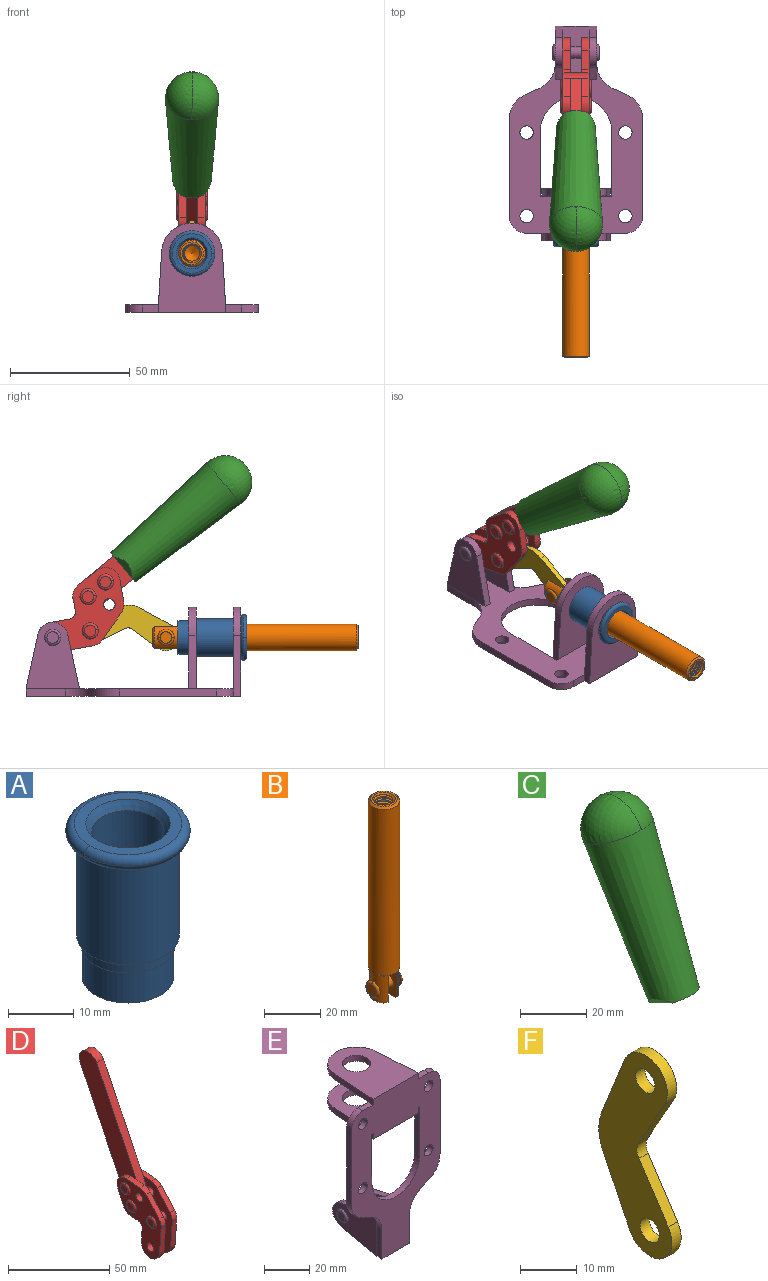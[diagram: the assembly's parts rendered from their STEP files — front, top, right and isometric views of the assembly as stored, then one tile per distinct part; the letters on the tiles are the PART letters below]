
ASSEMBLY  parts=6 mates=6
PART A: 15 faces, bbox 20.6x20.6x28.7 mm
  f0: torus R=8.26mm, axis (0,0,1), area 56.8mm2, adj f1,f10,f12
  f1: torus R=8.26mm, axis (0,0,1), area 56.8mm2, adj f0,f6,f13
  f2: cylinder r=5.59mm len=25.91mm, axis (0,0,1), area 909.6mm2, adj f3,f4
  f3: cone r=6.86mm half-angle=45deg, axis (0,0,-1), area 70.2mm2, adj f2,f14
  f4: cone r=6.47mm half-angle=30deg, axis (0,0,1), area 66.7mm2, adj f2,f13
  f5: cylinder r=7.04mm len=14.07mm, axis (0,0,1), area 252.6mm2, adj f11,f14
  f6: torus R=8.26mm, axis (0,0,1), area 56.8mm2, adj f1,f12,f13
  f7: cylinder r=7.16mm len=14.33mm, axis (0,0,1), area 91.5mm2, adj f9,f11
  f8: cylinder r=7.86mm len=18.42mm, axis (0,0,1), area 909.6mm2, adj f9,f10
  f9: plane 15.72x15.72mm, normal (0,0,-1), area 33mm2, adj f7,f8
  f10: plane 16.51x16.51mm, normal (0,0,-1), area 19.9mm2, adj f0,f8,f12
  f11: plane 14.33x14.33mm, normal (0,0,-1), area 5.7mm2, adj f5,f7
  f12: torus R=8.26mm, axis (0,0,1), area 56.8mm2, adj f0,f6,f10
  f13: plane 16.51x16.51mm, normal (0,0,1), area 82.7mm2, adj f1,f4,f6
  f14: plane 14.07x14.07mm, normal (0,0,-1), area 7.8mm2, adj f3,f5
PART B: 48 faces, bbox 12.6x11.1x86.1 mm
  f0: torus R=2.41mm, axis (-1,0,0), area 15mm2, adj f30,f32,f34
  f1: torus R=2.41mm, axis (-1,0,0), area 15mm2, adj f29,f31,f33
  f2: cylinder r=5.54mm len=72.39mm, axis (0,0,1), area 2518.5mm2, adj f3,f4,f42,f43
  f3: cone r=5.54mm half-angle=45deg, axis (0,0,1), area 7.6mm2, adj f2,f5,f41
  f4: cone r=5.54mm half-angle=45deg, axis (0,0,-1), area 34.9mm2, adj f2,f39
  f5: cylinder r=5.08mm len=11.48mm, axis (0,0,1), area 108.3mm2, adj f3,f7,f8,f41
  f6: cylinder r=2.41mm len=4.83mm, axis (-1,0,0), area 71.2mm2, adj f40,f41
  f7: cylinder r=2.41mm len=4.83mm, axis (-1,0,0), area 7.6mm2, adj f5,f34
  f8: cone r=5.08mm half-angle=45deg, axis (0,0,1), area 10.6mm2, adj f5,f37,f41
  f9: cone r=3.98mm half-angle=45deg, axis (0,0,1), area 17.6mm2, adj f27,f39,f45,f46,f47
  f10: cylinder r=2.41mm len=4.83mm, axis (-1,0,0), area 7.6mm2, adj f33,f38
  f11: cylinder r=3.2mm len=6.4mm, axis (0,0,1), area 78.4mm2, adj f12,f28,f44,f45,f47
  f12: cylinder r=3.2mm len=6.4mm, axis (0,0,1), area 10.5mm2, adj f11,f13,f45,f47
  f13: cylinder r=3.2mm len=6.4mm, axis (0,0,1), area 10.5mm2, adj f12,f14,f45,f47
  f14: cylinder r=3.2mm len=6.4mm, axis (0,0,1), area 10.5mm2, adj f13,f15,f45,f47
  f15: cylinder r=3.2mm len=6.4mm, axis (0,0,1), area 10.5mm2, adj f14,f16,f45,f47
  f16: cylinder r=3.2mm len=6.4mm, axis (0,0,1), area 10.5mm2, adj f15,f17,f45,f47
  f17: cylinder r=3.2mm len=6.4mm, axis (0,0,1), area 10.5mm2, adj f16,f18,f45,f47
  f18: cylinder r=3.2mm len=6.4mm, axis (0,0,1), area 10.5mm2, adj f17,f19,f45,f47
  f19: cylinder r=3.2mm len=6.4mm, axis (0,0,1), area 10.5mm2, adj f18,f20,f45,f47
  f20: cylinder r=3.2mm len=6.4mm, axis (0,0,1), area 10.5mm2, adj f19,f21,f45,f47
  f21: cylinder r=3.2mm len=6.4mm, axis (0,0,1), area 10.5mm2, adj f20,f22,f45,f47
  f22: cylinder r=3.2mm len=6.4mm, axis (0,0,1), area 10.5mm2, adj f21,f23,f45,f47
  f23: cylinder r=3.2mm len=6.4mm, axis (0,0,1), area 10.5mm2, adj f22,f24,f45,f47
  f24: cylinder r=3.2mm len=6.4mm, axis (0,0,1), area 10.5mm2, adj f23,f25,f45,f47
  f25: cylinder r=3.2mm len=6.4mm, axis (0,0,1), area 10.5mm2, adj f24,f26,f45,f47
  f26: cylinder r=3.2mm len=6.4mm, axis (0,0,1), area 10.5mm2, adj f25,f27,f45,f47
  f27: cylinder r=3.2mm len=6.4mm, axis (0,0,1), area 7.4mm2, adj f9,f26,f45,f47
  f28: cone r=3.2mm half-angle=60deg, axis (0,0,1), area 37.2mm2, adj f11
  f29: plane 4.83x4.83mm, normal (-1,0,0), area 18.3mm2, adj f1,f31
  f30: plane 4.83x4.83mm, normal (1,0,0), area 18.3mm2, adj f0,f32
  f31: torus R=2.41mm, axis (-1,0,0), area 15mm2, adj f1,f29,f33
  f32: torus R=2.41mm, axis (-1,0,0), area 15mm2, adj f0,f30,f34
  f33: plane 6.83x6.83mm, normal (1,0,0), area 18.3mm2, adj f1,f10,f31
  f34: plane 6.83x6.83mm, normal (-1,0,0), area 18.3mm2, adj f0,f7,f32
  f35: cone r=5.08mm half-angle=45deg, axis (0,0,1), area 10.6mm2, adj f36,f38,f40
  f36: plane 7.25x1.97mm, normal (0,0,-1), area 10mm2, adj f35,f40
  f37: plane 7.25x1.97mm, normal (0,0,-1), area 10mm2, adj f8,f41
  f38: cylinder r=5.08mm len=11.48mm, axis (0,0,1), area 108.3mm2, adj f10,f35,f40,f42
  f39: plane 9.55x9.55mm, normal (0,0,1), area 22mm2, adj f4,f9
  f40: plane 12.76x10.09mm, normal (1,0,0), area 95.7mm2, adj f6,f35,f36,f38,f42,f43
  f41: plane 12.76x10.09mm, normal (-1,0,0), area 95.7mm2, adj f3,f5,f6,f8,f37,f43
  f42: cone r=5.54mm half-angle=45deg, axis (0,0,1), area 7.6mm2, adj f2,f38,f40
  f43: plane 11.07x4.7mm, normal (0,0,-1), area 50.4mm2, adj f2,f40,f41
  f44: plane 0.89x0.62mm, normal (-1,0,0), area 0.3mm2, adj f11,f45,f46,f47
  f45: bspline ~24.8x7.63mm, area 266.6mm2, adj f9,f11,f12,f13,f14,f15,f16,f17
  f46: bspline ~24.87x7.63mm, area 73.6mm2, adj f9,f44,f45,f47
  f47: bspline ~24.98x7.63mm, area 272.5mm2, adj f9,f11,f12,f13,f14,f15,f16,f17
PART C: 11 faces, bbox 22.3x42.6x64.5 mm
  f0: sphere r=11.13mm, area 411.4mm2, adj f1,f8
  f1: cone r=11.11mm half-angle=3.3deg, axis (0,0.44,0.9), area 3251.8mm2, adj f0,f7,f8,f9,f10
  f2: cylinder r=6.16mm len=11.7mm, axis (1,0,0), area 89.5mm2, adj f3,f4,f5,f6
  f3: plane 60.23x36.75mm, normal (-1,0,0), area 763.6mm2, adj f2,f4,f6,f10
  f4: plane 51.37x25.05mm, normal (0,0.9,-0.44), area 264.2mm2, adj f2,f3,f5,f10
  f5: plane 60.23x36.75mm, normal (1,0,0), area 763.6mm2, adj f2,f4,f6,f10
  f6: plane 51.37x25.05mm, normal (0,-0.9,0.44), area 264.2mm2, adj f2,f3,f5,f10
  f7: plane 9.95x5.95mm, normal (0.71,-0.31,-0.64), area 25.8mm2, adj f1,f10
  f8: sphere r=11.13mm, area 411.4mm2, adj f0,f1
  f9: plane 9.95x5.95mm, normal (-0.71,-0.31,-0.64), area 25.8mm2, adj f1,f10
  f10: plane 14.27x11.38mm, normal (0,-0.44,-0.9), area 106.7mm2, adj f1,f3,f4,f5,f6,f7,f9
PART D: 59 faces, bbox 12.9x60.2x99.6 mm
  f0: torus R=2.39mm, axis (-1,0,0), area 14.9mm2, adj f20,f43,f51
  f1: torus R=2.39mm, axis (-1,0,0), area 14.9mm2, adj f19,f42,f51
  f2: torus R=2.39mm, axis (-1,0,0), area 14.9mm2, adj f18,f35,f51
  f3: torus R=2.39mm, axis (-1,0,0), area 14.9mm2, adj f14,f17,f23
  f4: torus R=2.39mm, axis (-1,0,0), area 14.9mm2, adj f13,f16,f23
  f5: torus R=2.39mm, axis (-1,0,0), area 14.9mm2, adj f12,f15,f23
  f6: cylinder r=2.39mm len=4.78mm, axis (1,0,0), area 46.5mm2, adj f48,f50,f51
  f7: cylinder r=2.39mm len=4.78mm, axis (1,0,0), area 46.5mm2, adj f50,f51
  f8: cylinder r=6.35mm len=12.68mm, axis (1,0,0), area 61.8mm2, adj f38,f39,f50,f51
  f9: cylinder r=2.39mm len=4.78mm, axis (-1,0,0), area 70.5mm2, adj f46,f50
  f10: cylinder r=2.39mm len=4.78mm, axis (-1,0,0), area 46.5mm2, adj f23,f45,f46
  f11: cylinder r=2.39mm len=4.78mm, axis (-1,0,0), area 46.5mm2, adj f23,f46
  f12: plane 4.78x4.78mm, normal (1,0,0), area 17.9mm2, adj f5,f15
  f13: plane 4.78x4.78mm, normal (1,0,0), area 17.9mm2, adj f4,f16
  f14: plane 4.78x4.78mm, normal (1,0,0), area 17.9mm2, adj f3,f17
  f15: torus R=2.39mm, axis (-1,0,0), area 14.9mm2, adj f5,f12,f23
  f16: torus R=2.39mm, axis (-1,0,0), area 14.9mm2, adj f4,f13,f23
  f17: torus R=2.39mm, axis (-1,0,0), area 14.9mm2, adj f3,f14,f23
  f18: plane 4.78x4.78mm, normal (-1,0,0), area 17.9mm2, adj f2,f35
  f19: plane 4.78x4.78mm, normal (-1,0,0), area 17.9mm2, adj f1,f42
  f20: plane 4.78x4.78mm, normal (-1,0,0), area 17.9mm2, adj f0,f43
  f21: plane 2.26x0.2mm, normal (1,0,0), area 0.2mm2, adj f31,f44
  f22: plane 2.26x0.2mm, normal (-1,0,0), area 0.2mm2, adj f41,f44
  f23: plane 39.37x30.77mm, normal (1,0,0), area 565.5mm2, adj f3,f4,f5,f10,f11,f15,f16,f17
  f24: cylinder r=6.1mm len=4.15mm, axis (-1,0,0), area 14.7mm2, adj f23,f25,f32,f46
  f25: plane 10.25x9.01mm, normal (0,-0.75,0.66), area 42.3mm2, adj f23,f24,f26,f46
  f26: cylinder r=6.35mm len=4.64mm, axis (-1,0,0), area 15.6mm2, adj f23,f25,f27,f46
  f27: plane 15.84x3.1mm, normal (0,-1,-0.07), area 49.2mm2, adj f23,f26,f28,f46
  f28: cylinder r=6.35mm len=12.68mm, axis (-1,0,0), area 61.8mm2, adj f23,f27,f29,f46
  f29: plane 8.11x3.1mm, normal (0,1,0.07), area 25.2mm2, adj f23,f28,f30,f46
  f30: cylinder r=3.05mm len=3.25mm, axis (-1,0,0), area 14.8mm2, adj f23,f29,f31,f46
  f31: plane 5.99x3.1mm, normal (0,0.07,-1), area 18.6mm2, adj f21,f23,f30,f44,f46
  f32: plane 9.5x3.1mm, normal (0,-0.07,1), area 29.5mm2, adj f23,f24,f33,f46,f47
  f33: cylinder r=6.1mm len=8.63mm, axis (-1,0,0), area 39.1mm2, adj f23,f32,f34,f47
  f34: plane 8.65x3.96mm, normal (0,0.91,-0.42), area 29.5mm2, adj f23,f33,f44,f47
  f35: torus R=2.39mm, axis (-1,0,0), area 14.9mm2, adj f2,f18,f51
  f36: plane 10.25x9.01mm, normal (0,-0.75,0.66), area 42.3mm2, adj f37,f49,f50,f51
  f37: cylinder r=6.35mm len=4.64mm, axis (1,0,0), area 15.6mm2, adj f36,f38,f50,f51
  f38: plane 15.84x3.1mm, normal (0,-1,-0.07), area 49.2mm2, adj f8,f37,f50,f51
  f39: plane 8.11x3.1mm, normal (0,1,0.07), area 25.2mm2, adj f8,f40,f50,f51
  f40: cylinder r=3.05mm len=3.25mm, axis (1,0,0), area 14.8mm2, adj f39,f41,f50,f51
  f41: plane 5.99x3.1mm, normal (0,0.07,-1), area 18.6mm2, adj f22,f40,f44,f50,f51
  f42: torus R=2.39mm, axis (-1,0,0), area 14.9mm2, adj f1,f19,f51
  f43: torus R=2.39mm, axis (-1,0,0), area 14.9mm2, adj f0,f20,f51
  f44: cylinder r=6.35mm len=12.12mm, axis (-1,0,0), area 128.9mm2, adj f21,f22,f23,f31,f34,f41,f46,f47
  f45: plane 2.65x1.35mm, normal (1,0,0), area 1mm2, adj f10,f55
  f46: plane 39.08x20.42mm, normal (-1,0,0), area 412.5mm2, adj f9,f10,f11,f24,f25,f26,f27,f28
  f47: plane 77.62x39.82mm, normal (1,0,0), area 850mm2, adj f32,f33,f34,f44,f53,f54,f55
  f48: plane 2.65x1.35mm, normal (-1,0,0), area 1mm2, adj f6,f55
  f49: cylinder r=6.1mm len=4.15mm, axis (1,0,0), area 14.7mm2, adj f36,f50,f51,f56
  f50: plane 39.08x20.42mm, normal (1,0,0), area 412.5mm2, adj f6,f7,f8,f9,f36,f37,f38,f39
  f51: plane 39.37x30.77mm, normal (-1,0,0), area 565.5mm2, adj f0,f1,f2,f6,f7,f8,f35,f36
  f52: plane 8.65x3.96mm, normal (0,0.91,-0.42), area 29.5mm2, adj f44,f51,f57,f58
  f53: plane 68.49x33.4mm, normal (0,0.9,-0.44), area 358.1mm2, adj f44,f47,f54,f58
  f54: cylinder r=6.35mm len=12.06mm, axis (1,0,0), area 93.7mm2, adj f47,f53,f55,f58
  f55: plane 68.49x33.4mm, normal (0,-0.9,0.44), area 358.1mm2, adj f44,f45,f46,f47,f48,f50,f54,f58
  f56: plane 9.5x3.1mm, normal (0,-0.07,1), area 29.5mm2, adj f49,f50,f51,f57,f58
  f57: cylinder r=6.1mm len=8.63mm, axis (1,0,0), area 39.1mm2, adj f51,f52,f56,f58
  f58: plane 77.62x39.82mm, normal (-1,0,0), area 850mm2, adj f44,f52,f53,f54,f55,f56,f57
PART E: 55 faces, bbox 55.7x37.4x89.8 mm
  f0: torus R=2.41mm, axis (-1,0,0), area 15mm2, adj f11,f15,f25
  f1: torus R=2.41mm, axis (-1,0,0), area 15mm2, adj f10,f12,f22
  f2: cylinder r=2.78mm len=5.56mm, axis (0,-1,0), area 54.2mm2, adj f30,f54
  f3: cylinder r=14.99mm len=29.97mm, axis (0,-1,0), area 145.9mm2, adj f30,f49,f53,f54
  f4: cylinder r=2.78mm len=5.56mm, axis (0,-1,0), area 54.2mm2, adj f30,f54
  f5: cylinder r=2.78mm len=5.56mm, axis (0,-1,0), area 54.2mm2, adj f30,f54
  f6: cylinder r=2.78mm len=5.56mm, axis (0,-1,0), area 54.2mm2, adj f30,f54
  f7: cylinder r=6.35mm len=12.7mm, axis (0,0,1), area 123.6mm2, adj f27,f51
  f8: cylinder r=6.35mm len=12.7mm, axis (0,0,-1), area 124.7mm2, adj f21,f35
  f9: cylinder r=2.41mm len=11.18mm, axis (-1,0,0), area 169.4mm2, adj f16,f19
  f10: plane 4.83x4.83mm, normal (1,0,0), area 18.3mm2, adj f1,f12
  f11: plane 4.83x4.83mm, normal (-1,0,0), area 18.3mm2, adj f0,f15
  f12: torus R=2.41mm, axis (-1,0,0), area 15mm2, adj f1,f10,f22
  f13: cylinder r=6.35mm len=12.41mm, axis (1,0,0), area 53.4mm2, adj f18,f19,f22,f23
  f14: cylinder r=6.35mm len=12.41mm, axis (-1,0,0), area 53.4mm2, adj f16,f17,f24,f25
  f15: torus R=2.41mm, axis (-1,0,0), area 15mm2, adj f0,f11,f25
  f16: plane 27.86x22.35mm, normal (1,0,0), area 425.4mm2, adj f9,f14,f17,f24,f30
  f17: plane 22.86x4.97mm, normal (0,0.21,0.98), area 72.5mm2, adj f14,f16,f25,f30
  f18: plane 22.86x4.97mm, normal (0,0.21,0.98), area 72.5mm2, adj f13,f19,f22,f30
  f19: plane 27.86x22.35mm, normal (-1,0,0), area 425.4mm2, adj f9,f13,f18,f23,f30
  f20: cylinder r=12.7mm len=25.35mm, axis (0,0,-1), area 119.8mm2, adj f21,f34,f35,f36
  f21: plane 34.21x28.07mm, normal (0,0,-1), area 702.4mm2, adj f8,f20,f30,f34,f36
  f22: plane 27.96x22.45mm, normal (1,0,0), area 407.2mm2, adj f1,f12,f13,f18,f23,f30,f42,f43
  f23: plane 22.86x4.97mm, normal (0,0.21,-0.98), area 72.5mm2, adj f13,f19,f22,f44
  f24: plane 22.86x4.97mm, normal (0,0.21,-0.98), area 72.5mm2, adj f14,f16,f25,f44
  f25: plane 27.86x22.35mm, normal (-1,0,0), area 407.1mm2, adj f0,f14,f15,f17,f24,f30,f45,f46
  f26: plane 3.1x0.95mm, normal (0,0,-1), area 2.7mm2, adj f30,f49,f50,f54
  f27: plane 34.21x28.07mm, normal (0,0,1), area 702.4mm2, adj f7,f28,f30,f50,f52
  f28: cylinder r=12.7mm len=25.35mm, axis (0,0,1), area 118.8mm2, adj f27,f50,f51,f52
  f29: plane 3.1x0.95mm, normal (0,0,-1), area 2.7mm2, adj f30,f52,f53,f54
  f30: plane 86.54x55.63mm, normal (0,1,0), area 2362.9mm2, adj f2,f3,f4,f5,f6,f16,f17,f18
  f31: plane 40.56x3.1mm, normal (-1,0,0), area 125.7mm2, adj f30,f32,f48,f54
  f32: cylinder r=7.11mm len=7.11mm, axis (0,-1,0), area 34.6mm2, adj f30,f31,f33,f54
  f33: plane 6.67x3.1mm, normal (0,0,1), area 20.4mm2, adj f30,f32,f34,f54
  f34: plane 25.39x3.13mm, normal (-1,0.06,0), area 79.5mm2, adj f20,f21,f33,f35,f54
  f35: plane 37.31x28.45mm, normal (0,0,1), area 789.9mm2, adj f8,f20,f34,f36,f54
  f36: plane 25.39x3.13mm, normal (1,0.06,0), area 79.5mm2, adj f20,f21,f35,f37,f54
  f37: plane 6.67x3.1mm, normal (0,0,1), area 20.4mm2, adj f30,f36,f38,f54
  f38: cylinder r=7.11mm len=7.11mm, axis (0,-1,0), area 34.6mm2, adj f30,f37,f39,f54
  f39: plane 40.56x3.1mm, normal (1,0,0), area 125.7mm2, adj f30,f38,f40,f54
  f40: cylinder r=11.18mm len=10.16mm, axis (0,-1,0), area 39.5mm2, adj f30,f39,f41,f54
  f41: plane 6.09x3.1mm, normal (0.42,0,-0.91), area 20.8mm2, adj f30,f40,f42,f54
  f42: cylinder r=11.18mm len=9.41mm, axis (0,-1,0), area 37.2mm2, adj f22,f30,f41,f43,f54
  f43: plane 16.5x3.1mm, normal (1,0,0), area 51.1mm2, adj f22,f42,f44,f54
  f44: plane 17.37x3.1mm, normal (0,0,-1), area 53.8mm2, adj f23,f24,f30,f43,f45,f54
  f45: plane 16.5x3.1mm, normal (-1,0,0), area 51.1mm2, adj f25,f44,f46,f54
  f46: cylinder r=11.18mm len=9.41mm, axis (0,-1,0), area 37.2mm2, adj f25,f30,f45,f47,f54
  f47: plane 6.09x3.1mm, normal (-0.42,0,-0.91), area 20.8mm2, adj f30,f46,f48,f54
  f48: cylinder r=11.18mm len=10.16mm, axis (0,-1,0), area 39.5mm2, adj f30,f31,f47,f54
  f49: plane 26.54x3.1mm, normal (-1,0,0), area 82.3mm2, adj f3,f26,f30,f54
  f50: plane 25.39x3.1mm, normal (1,0.06,0), area 78.8mm2, adj f26,f27,f28,f51,f54
  f51: plane 37.31x28.45mm, normal (0,0,-1), area 789.9mm2, adj f7,f28,f50,f52,f54
  f52: plane 25.39x3.1mm, normal (-1,0.06,0), area 78.8mm2, adj f27,f28,f29,f51,f54
  f53: plane 26.54x3.1mm, normal (1,0,0), area 82.3mm2, adj f3,f29,f30,f54
  f54: plane 89.66x55.63mm, normal (0,-1,0), area 2678.5mm2, adj f2,f3,f4,f5,f6,f26,f29,f31
PART F: 12 faces, bbox 2.3x18.2x42.8 mm
  f0: cylinder r=2.4mm len=4.8mm, axis (1,0,0), area 34.9mm2, adj f4,f11
  f1: cylinder r=10.41mm len=8.47mm, axis (1,0,0), area 20.2mm2, adj f4,f9,f10,f11
  f2: cylinder r=3.05mm len=3.16mm, axis (1,0,0), area 7.7mm2, adj f4,f6,f7,f11
  f3: cylinder r=2.4mm len=4.8mm, axis (1,0,0), area 34.9mm2, adj f4,f11
  f4: plane 42.81x18.23mm, normal (-1,0,0), area 414.1mm2, adj f0,f1,f2,f3,f5,f6,f7,f8
  f5: cylinder r=5.54mm len=10.67mm, axis (1,0,0), area 41.8mm2, adj f4,f6,f10,f11
  f6: plane 11.66x6.53mm, normal (0,-0.87,-0.49), area 30.9mm2, adj f2,f4,f5,f11
  f7: plane 11.17x7.33mm, normal (0,-0.84,0.55), area 30.9mm2, adj f2,f4,f8,f11
  f8: cylinder r=5.54mm len=10.51mm, axis (1,0,0), area 41.8mm2, adj f4,f7,f9,f11
  f9: plane 13.67x6.67mm, normal (0,0.9,-0.44), area 35.1mm2, adj f1,f4,f8,f11
  f10: plane 14.1x5.7mm, normal (0,0.93,0.37), area 35.1mm2, adj f1,f4,f5,f11
  f11: plane 42.81x18.23mm, normal (1,0,0), area 414.1mm2, adj f0,f1,f2,f3,f5,f6,f7,f8
PLACE A rot(axis=(1,0,0),90deg) t=(0,0,0)mm
PLACE B rot(axis=(1,0,0),90deg) t=(0,0.29,0)mm
PLACE C rot(axis=(1,0,0),76.2deg) t=(0,-4.95,8.38)mm
PLACE D rot(axis=(1,0,0),76.2deg) t=(0,-4.95,8.38)mm
PLACE E rot(axis=(1,0,0),90deg) t=(0,0,0)mm fixed
PLACE F rot(axis=(0,0.69,0.72),180deg) t=(0,2.24,1.96)mm
MATE revolute F.f5 <-> D.f4  axis (-1,0,0) through (0,16.45,27.32)mm
MATE revolute D.f7 <-> E.f0  axis (-1,0,0) through (0,32.09,24.61)mm
MATE revolute F.f3 <-> B.f6  axis (-1,0,0) through (0,-15.18,24.61)mm
MATE fastened C.f2 <-> D.f54  axis (1,0,0) through (0,-41.17,90.44)mm
MATE slider B.f2 <-> A.f2  axis (0,-1,0) through (0,-58.49,24.61)mm
MATE fastened A.f0 <-> E.f7  axis (0,1,0) through (0,-46.39,24.61)mm
